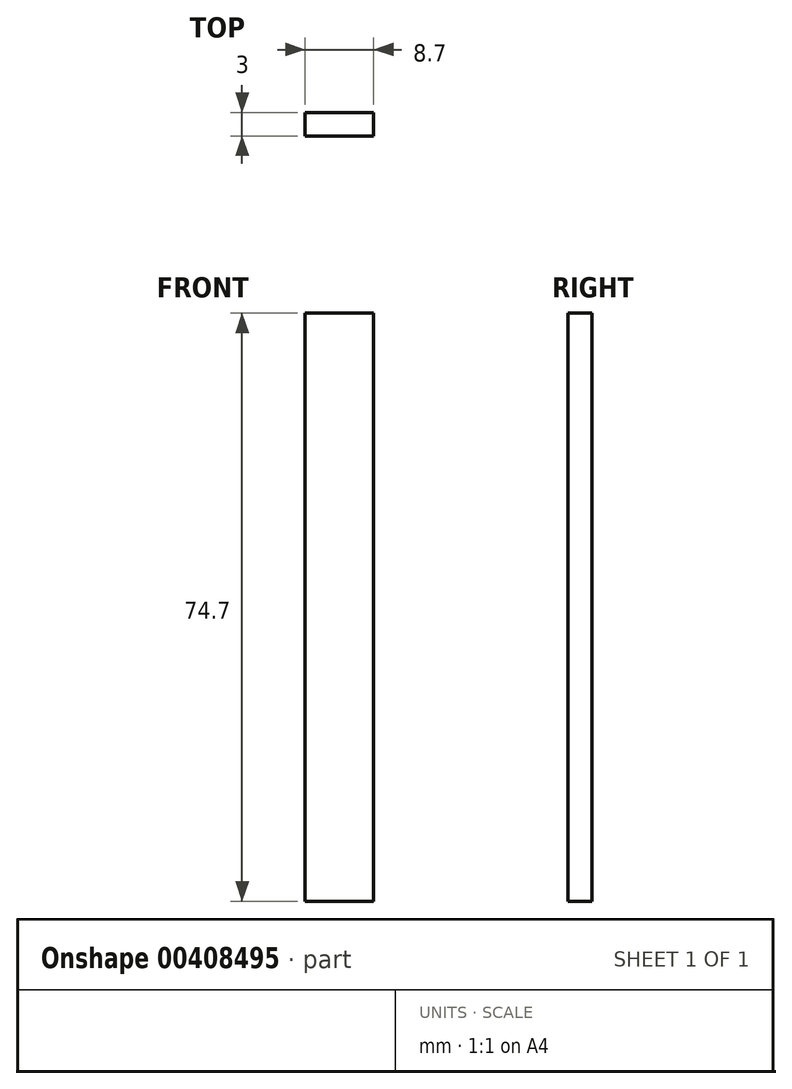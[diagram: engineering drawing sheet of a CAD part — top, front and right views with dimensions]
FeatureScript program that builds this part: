
annotation { "Feature Type Name" : "Feature", "Feature Type Description" : "" }
export const myFeature = defineFeature(function(context is Context, id is Id, definition is map)
    precondition{}
    {
        {
            var Q0;
            Q0=qCreatedBy(makeId("Front.planeOp"),FACE);
            var sketch = newSketch(context, id + "F0", { "sketchPlane" : qUnion([Q0])});
            skLineSegment(sketch, "E0.bottom", {"start": v(16.1, 74.7) * mm, "end": v(24.8, 74.7) * mm});
            skLineSegment(sketch, "E0.top", {"start": v(16.1, 0) * mm, "end": v(24.8, 0) * mm});
            skLineSegment(sketch, "E0.left", {"start": v(16.1, 74.7) * mm, "end": v(16.1, 0) * mm});
            skLineSegment(sketch, "E0.right", {"start": v(24.8, 74.7) * mm, "end": v(24.8, 0) * mm});
            skPoint(sketch, "E1.top.end.orphan", {"position": v(-42.3, 0) * mm});
            skSolve(sketch);
        }
        {
            var Q0;
            Q0 = qSketchRegion(id + "F0", true);
            extrude(context, id + "F1", {"entities" : qUnion([Q0]), "depth" : 3 * mm});
        }
        {
            var Q0;
            Q0 = qSketchRegion(id + "F0", true);
            extrude(context, id + "F2", {"entities" : qUnion([Q0]), "operationType" : NewBodyOperationType.ADD, "depth" : 3 * mm});
        }
    });
